# Revit family: Klemmstück für Gitterrinne - GKT 38 G
name_source: partatom
category: Generic Models
revit_build: Autodesk Revit 2017 (Build: 20190508_0315(x64)
units: mm (PartAtom-declared; Revit-internal decimal feet)

## family parameters
Always vertical = Yes
Can host rebar = No
Cut with Voids When Loaded = No
Part Type = Normal
Room Calculation Point = No
Round Connector Dimension = Use Diameter
Shared = No
Work Plane-Based = No

## types (4) — shared parameters
Manufacturer = OBO BETTERMANN
URL = http://www.obo-bettermann.com

## per-type parameters (varying)
| type | GTIN | Manufacturer Art.No. | Material |
| GKT 38 G | 4012196307937 | 6017037 | Electro-galvanised |
| GKT 38 FT | 4012196013630 | 6017061 | Hot-dip galvanised |
| GKT 38 A2 | 4012196013579 | 6017045 | Stainless steel, A2 |
| GKT 38 A4 | 4012196120499 | 6017092 | Stainless steel, A4 |

note: column(s) folded — value = type name in every type: Article Type

## geometry (parser evidence)
native form markers: Sweep x2
no freeform markers — native parametric forms only
